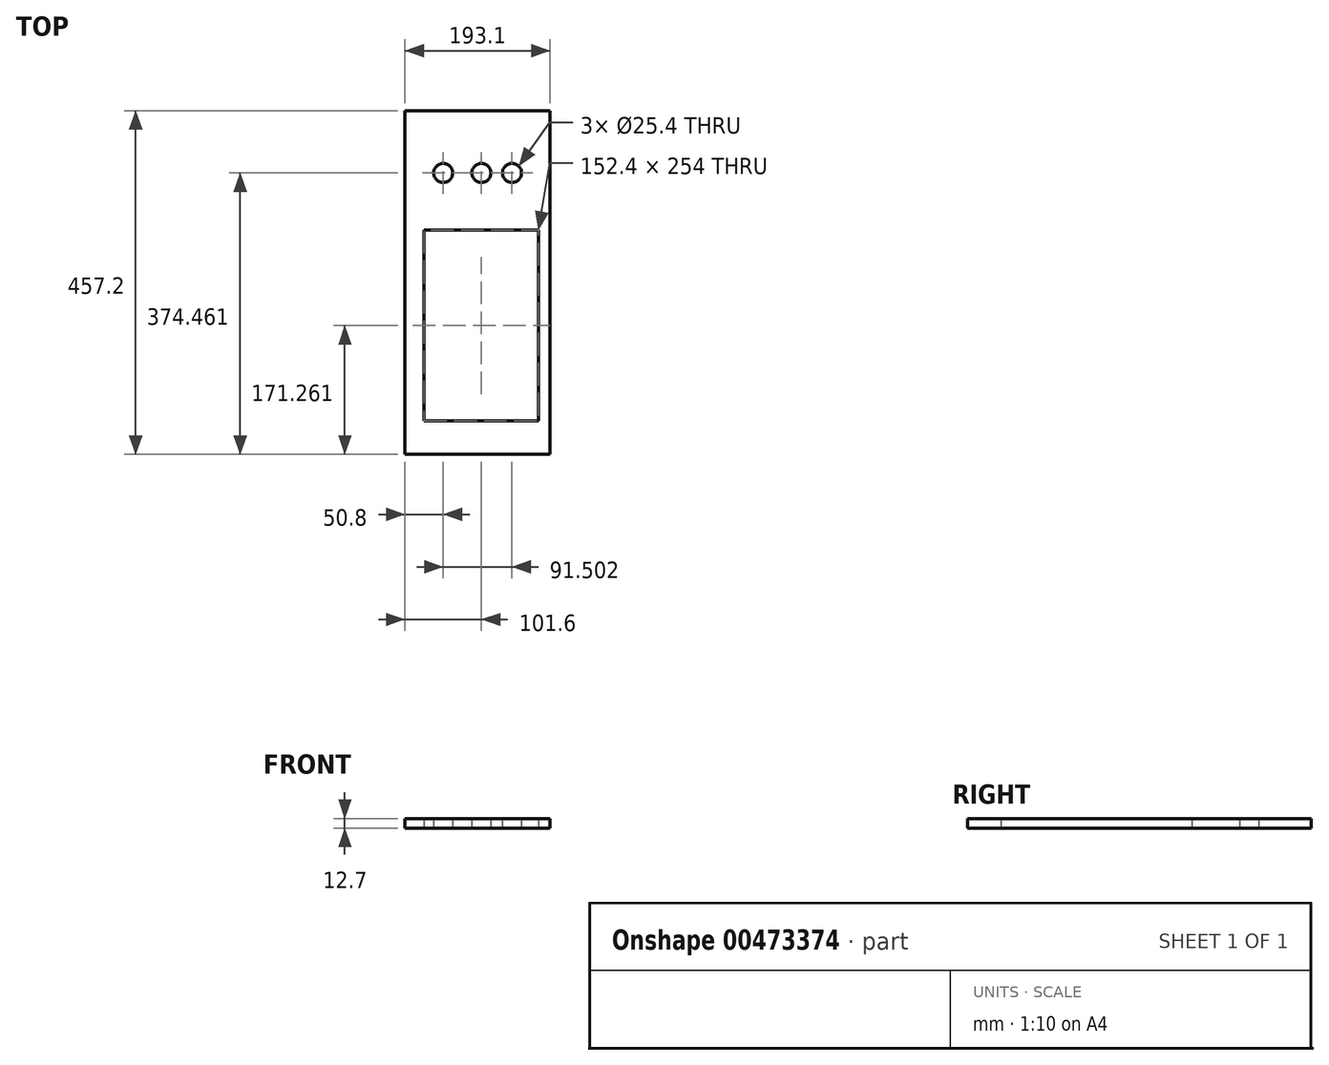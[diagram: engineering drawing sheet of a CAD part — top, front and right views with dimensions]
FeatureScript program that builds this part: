
annotation { "Feature Type Name" : "Feature", "Feature Type Description" : "" }
export const myFeature = defineFeature(function(context is Context, id is Id, definition is map)
    precondition{}
    {
        {
            var Q0;
            Q0=qCreatedBy(makeId("Top.planeOp"),FACE);
            var sketch = newSketch(context, id + "F0", { "sketchPlane" : qUnion([Q0])});
            skLineSegment(sketch, "E0", {"start": v(0, 0) * mm, "end": v(0, 457.2) * mm});
            skLineSegment(sketch, "E1", {"start": v(0, 457.2) * mm, "end": v(193.1, 457.2) * mm});
            skLineSegment(sketch, "E2", {"start": v(193.1, 457.2) * mm, "end": v(193.1, 0) * mm});
            skLineSegment(sketch, "E3", {"start": v(193.1, 0) * mm, "end": v(0, 0) * mm});
            skLineSegment(sketch, "E4", {"start": v(25.4, 44.26) * mm, "end": v(177.8, 44.26) * mm});
            skLineSegment(sketch, "E5", {"start": v(25.4, 44.26) * mm, "end": v(25.4, 298.26) * mm});
            skLineSegment(sketch, "E6", {"start": v(177.8, 44.26) * mm, "end": v(177.8, 298.26) * mm});
            skLineSegment(sketch, "E7", {"start": v(25.4, 298.26) * mm, "end": v(177.8, 298.26) * mm});
            skCircle(sketch, "E8", {"center": v(50.8, 374.46) * mm, "radius": 12.7 * mm});
            skCircle(sketch, "E9", {"center": v(101.6, 374.46) * mm, "radius": 12.7 * mm});
            skCircle(sketch, "E10", {"center": v(142.3, 374.46) * mm, "radius": 12.7 * mm});
            skSolve(sketch);
        }
        {
            var Q0;
            Q0 = qSketchRegion(id + "F0", true);
            extrude(context, id + "F1", {"entities" : qUnion([Q0]), "depth" : 12.7 * mm});
        }
    });
